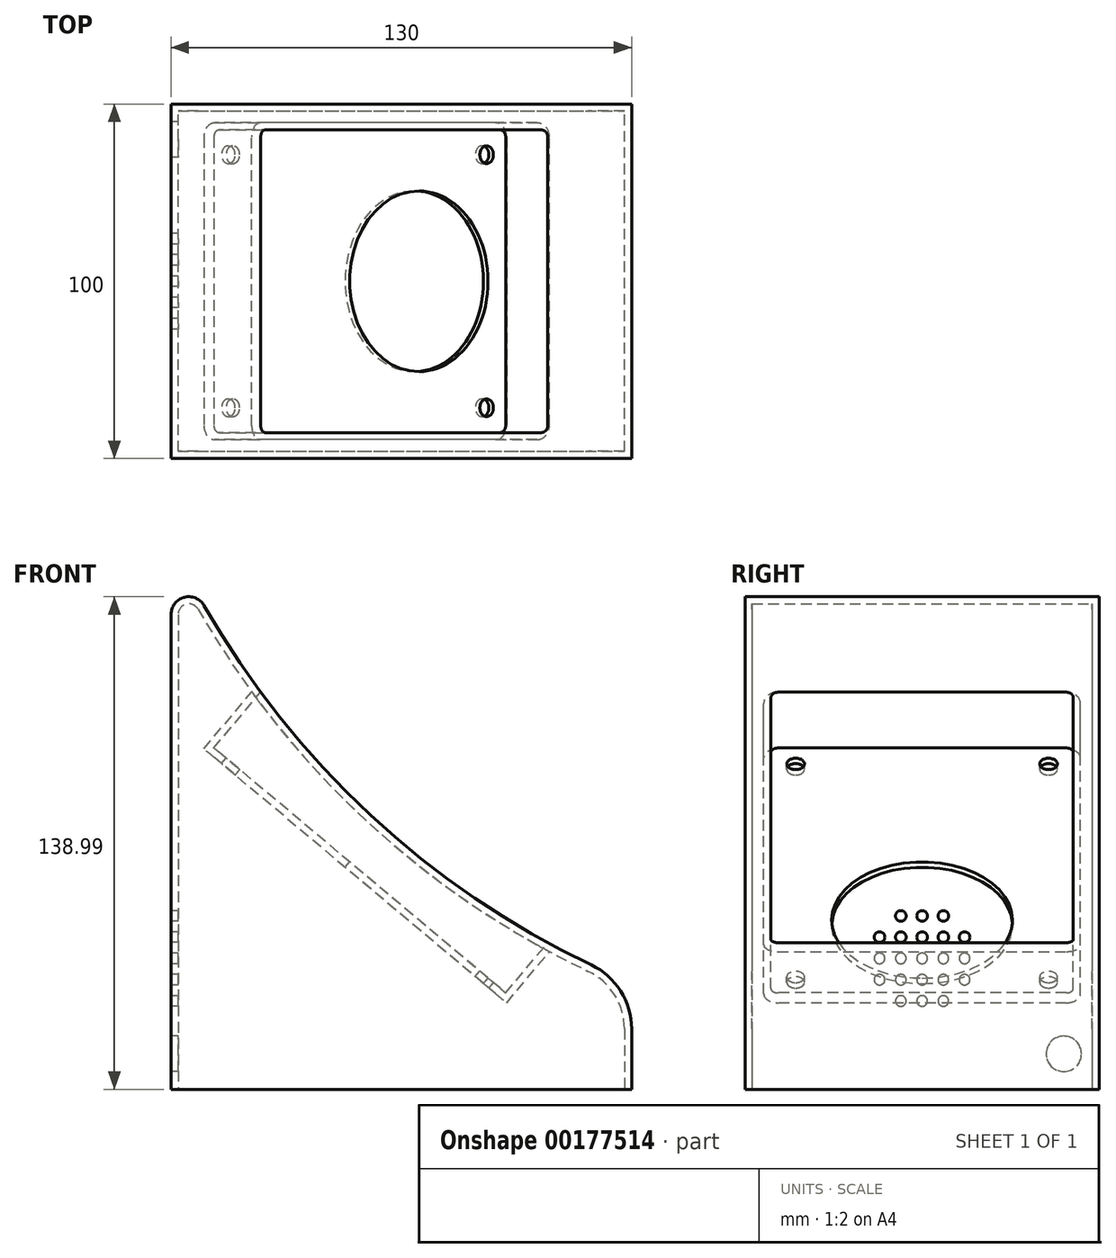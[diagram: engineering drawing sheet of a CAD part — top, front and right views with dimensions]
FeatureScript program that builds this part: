
annotation { "Feature Type Name" : "Feature", "Feature Type Description" : "" }
export const myFeature = defineFeature(function(context is Context, id is Id, definition is map)
    precondition{}
    {
        {
            var Q0;
            Q0=qCreatedBy(makeId("Front.planeOp"),FACE);
            var sketch = newSketch(context, id + "F0", { "sketchPlane" : qUnion([Q0])});
            skLineSegment(sketch, "E0", {"start": v(-84.02, -67.29) * mm, "end": v(45.98, -67.29) * mm});
            skPoint(sketch, "E1.visualSharp", {"position": v(-84.02, 87.14) * mm});
            skPoint(sketch, "E2.visualSharp", {"position": v(45.98, -37.29) * mm});
            skArc(sketch, "E3", {"start": v(-74.68, 69.19) * mm, "mid": v(-23.15, 5.98) * mm, "end": v(45.98, -37.29) * mm});
            skLineSegment(sketch, "E4", {"start": v(-84.02, 66.7) * mm, "end": v(-84.02, -67.29) * mm});
            skLineSegment(sketch, "E5", {"start": v(45.98, -37.29) * mm, "end": v(45.98, -67.29) * mm});
            skArc(sketch, "E6.filletArc", {"start": v(-74.68, 69.19) * mm, "mid": v(-80.3, 71.53) * mm, "end": v(-84.02, 66.7) * mm});
            skSolve(sketch);
        }
        {
            var Q0;
            Q0=makeQuery(id+"F0.imprint","IMPRINT",FACE,{"disambiguationData":[TD([[makeQuery(id+"F0.imprint","IMPRINT",EDGE,{"derivedFrom":sQuery(id+"F0.wireOp",EDGE,"E0")}),1.0]])]});
            extrude(context, id + "F1", {"entities" : qUnion([Q0]), "depth" : 100 * mm, "symmetric" : true});
        }
        {
            var Q0;
            Q0=makeQuery(id+"F1.opExtrude","SWEPT_EDGE",EDGE,{"disambiguationData":[OSD([sQuery(id+"F0.wireOp",EDGE,"E3"),sQuery(id+"F0.wireOp",EDGE,"E5")])]});
            cPlane(context, id + "F2", {"entities" : qUnion([Q0]), "cplaneType" : CPlaneType.LINE_ANGLE, "offset" : 25 * mm, "angle" : 40 * degree, "width" : 150 * mm, "height" : 150 * mm});
        }
        {
            var Q0;
            Q0=qCreatedBy(id+"F2.planeOp",FACE);
            var sketch = newSketch(context, id + "F3", { "sketchPlane" : qUnion([Q0])});
            skLineSegment(sketch, "E7.bottom", {"start": v(31.75, 42.7) * mm, "end": v(-71.75, 42.7) * mm});
            skLineSegment(sketch, "E7.top", {"start": v(31.75, -42.7) * mm, "end": v(-71.75, -42.7) * mm});
            skLineSegment(sketch, "E7.left", {"start": v(33.75, 40.7) * mm, "end": v(33.75, -40.7) * mm});
            skLineSegment(sketch, "E7.right", {"start": v(-73.75, 40.7) * mm, "end": v(-73.75, -40.7) * mm});
            skPoint(sketch, "E7.middle", {"position": v(-20, 0) * mm});
            skPoint(sketch, "E8.visualSharp", {"position": v(-73.75, -42.7) * mm});
            skArc(sketch, "E8.filletArc", {"start": v(-73.75, -40.7) * mm, "mid": v(-73.16, -42.11) * mm, "end": v(-71.75, -42.7) * mm});
            skPoint(sketch, "E9.visualSharp", {"position": v(-73.75, 42.7) * mm});
            skArc(sketch, "E9.filletArc", {"start": v(-71.75, 42.7) * mm, "mid": v(-73.16, 42.11) * mm, "end": v(-73.75, 40.7) * mm});
            skPoint(sketch, "E10.visualSharp", {"position": v(33.75, 42.7) * mm});
            skArc(sketch, "E10.filletArc", {"start": v(33.75, 40.7) * mm, "mid": v(33.16, 42.11) * mm, "end": v(31.75, 42.7) * mm});
            skPoint(sketch, "E11.visualSharp", {"position": v(33.75, -42.7) * mm});
            skArc(sketch, "E11.filletArc", {"start": v(31.75, -42.7) * mm, "mid": v(33.16, -42.11) * mm, "end": v(33.75, -40.7) * mm});
            skCircle(sketch, "E12", {"center": v(1.75, 0) * mm, "radius": 25.5 * mm});
            skCircle(sketch, "E13", {"center": v(-66.75, -35.7) * mm, "radius": 2.5 * mm});
            skCircle(sketch, "E14", {"center": v(-66.75, 35.7) * mm, "radius": 2.5 * mm});
            skCircle(sketch, "E15", {"center": v(26.75, 35.7) * mm, "radius": 2.5 * mm});
            skCircle(sketch, "E16", {"center": v(26.75, -35.7) * mm, "radius": 2.5 * mm});
            skSolve(sketch);
        }
        {
            var Q0;
            Q0=makeQuery(id+"F3.imprint","IMPRINT",FACE,{"disambiguationData":[TD([[makeQuery(id+"F3.imprint","IMPRINT",EDGE,{"derivedFrom":sQuery(id+"F3.wireOp",EDGE,"E7.bottom")}),1.0]])]});
            var Q1;
            Q1=makeQuery(id+"F3.imprint","IMPRINT",FACE,{"disambiguationData":[TD([[makeQuery(id+"F3.imprint","IMPRINT",EDGE,{"derivedFrom":sQuery(id+"F3.wireOp",EDGE,"E12")}),1.0]])]});
            var Q2;
            Q2=makeQuery(id+"F3.imprint","IMPRINT",FACE,{"disambiguationData":[TD([[makeQuery(id+"F3.imprint","IMPRINT",EDGE,{"derivedFrom":sQuery(id+"F3.wireOp",EDGE,"E14")}),1.0]])]});
            var Q3;
            Q3=makeQuery(id+"F3.imprint","IMPRINT",FACE,{"disambiguationData":[TD([[makeQuery(id+"F3.imprint","IMPRINT",EDGE,{"derivedFrom":sQuery(id+"F3.wireOp",EDGE,"E15")}),1.0]])]});
            var Q4;
            Q4=makeQuery(id+"F3.imprint","IMPRINT",FACE,{"disambiguationData":[TD([[makeQuery(id+"F3.imprint","IMPRINT",EDGE,{"derivedFrom":sQuery(id+"F3.wireOp",EDGE,"E16")}),1.0]])]});
            var Q5;
            Q5=makeQuery(id+"F3.imprint","IMPRINT",FACE,{"disambiguationData":[TD([[makeQuery(id+"F3.imprint","IMPRINT",EDGE,{"derivedFrom":sQuery(id+"F3.wireOp",EDGE,"E13")}),1.0]])]});
            extrude(context, id + "F4", {"entities" : qUnion([Q0, Q1, Q2, Q3, Q4, Q5]), "operationType" : NewBodyOperationType.REMOVE, "oppositeDirection" : true, "depth" : 25 * mm});
        }
        {
            var Q0;
            Q0=makeQuery(id+"F1.opExtrude","SWEPT_EDGE",EDGE,{"disambiguationData":[OSD([sQuery(id+"F0.wireOp",EDGE,"E3"),sQuery(id+"F0.wireOp",EDGE,"E5")])]});
            fillet(context, id + "F5", {"entities" : qUnion([Q0]), "radius" : 20 * mm, "tangentPropagation" : true, "allowEdgeOverflow" : false});
        }
        {
            var Q0;
            Q0=makeQuery(id+"F1.opExtrude","SWEPT_FACE",FACE,{"disambiguationData":[OSD([sQuery(id+"F0.wireOp",EDGE,"E0")])]});
            shell(context, id + "F6", {"entities" : qUnion([Q0]), "thickness" : 2 * mm});
        }
        {
            var Q0;
            Q0=makeQuery(id+"F3.imprint","IMPRINT",FACE,{"disambiguationData":[TD([[makeQuery(id+"F3.imprint","IMPRINT",EDGE,{"derivedFrom":sQuery(id+"F3.wireOp",EDGE,"E12")}),1.0]])]});
            var Q1;
            Q1=makeQuery(id+"F3.imprint","IMPRINT",FACE,{"disambiguationData":[TD([[makeQuery(id+"F3.imprint","IMPRINT",EDGE,{"derivedFrom":sQuery(id+"F3.wireOp",EDGE,"E14")}),1.0]])]});
            var Q2;
            Q2=makeQuery(id+"F3.imprint","IMPRINT",FACE,{"disambiguationData":[TD([[makeQuery(id+"F3.imprint","IMPRINT",EDGE,{"derivedFrom":sQuery(id+"F3.wireOp",EDGE,"E13")}),1.0]])]});
            var Q3;
            Q3=makeQuery(id+"F3.imprint","IMPRINT",FACE,{"disambiguationData":[TD([[makeQuery(id+"F3.imprint","IMPRINT",EDGE,{"derivedFrom":sQuery(id+"F3.wireOp",EDGE,"E15")}),1.0]])]});
            var Q4;
            Q4=makeQuery(id+"F3.imprint","IMPRINT",FACE,{"disambiguationData":[TD([[makeQuery(id+"F3.imprint","IMPRINT",EDGE,{"derivedFrom":sQuery(id+"F3.wireOp",EDGE,"E16")}),1.0]])]});
            extrude(context, id + "F7", {"entities" : qUnion([Q0, Q1, Q2, Q3, Q4]), "operationType" : NewBodyOperationType.REMOVE, "oppositeDirection" : true, "depth" : 40 * mm});
        }
        {
            var Q0;
            Q0=makeQuery(id+"F1.opExtrude","SWEPT_FACE",FACE,{"disambiguationData":[OSD([sQuery(id+"F0.wireOp",EDGE,"E4")])]});
            var sketch = newSketch(context, id + "F8", { "sketchPlane" : qUnion([Q0])});
            skCircle(sketch, "E17", {"center": v(0, -30.36) * mm, "radius": 25 * mm, "construction": true});
            skLineSegment(sketch, "E18", {"start": v(0, 0) * mm, "end": v(0, -62.03) * mm, "construction": true});
            skLineSegment(sketch, "E19", {"start": v(-40.29, -30.36) * mm, "end": v(40.58, -30.36) * mm, "construction": true});
            skLineSegment(sketch, "E20", {"start": v(-40.29, -24.36) * mm, "end": v(40.58, -24.36) * mm, "construction": true});
            skLineSegment(sketch, "E21", {"start": v(-40.29, -36.36) * mm, "end": v(40.58, -36.36) * mm, "construction": true});
            skLineSegment(sketch, "E22", {"start": v(-40.29, -42.36) * mm, "end": v(40.58, -42.36) * mm, "construction": true});
            skLineSegment(sketch, "E23", {"start": v(-40.29, -18.36) * mm, "end": v(40.58, -18.36) * mm, "construction": true});
            skLineSegment(sketch, "E24", {"start": v(-6, 0) * mm, "end": v(-6, -62.03) * mm, "construction": true});
            skLineSegment(sketch, "E25", {"start": v(6, 0) * mm, "end": v(6, -62.03) * mm, "construction": true});
            skLineSegment(sketch, "E26", {"start": v(12, 0) * mm, "end": v(12, -62.03) * mm, "construction": true});
            skLineSegment(sketch, "E27", {"start": v(-12, 0) * mm, "end": v(-12, -62.03) * mm, "construction": true});
            skCircle(sketch, "E28", {"center": v(0, -30.36) * mm, "radius": 1.5 * mm});
            skCircle(sketch, "E29", {"center": v(6, -30.36) * mm, "radius": 1.5 * mm});
            skCircle(sketch, "E30", {"center": v(12, -30.36) * mm, "radius": 1.5 * mm});
            skCircle(sketch, "E31", {"center": v(-6, -30.36) * mm, "radius": 1.5 * mm});
            skCircle(sketch, "E32", {"center": v(-12, -30.36) * mm, "radius": 1.5 * mm});
            skCircle(sketch, "E33", {"center": v(0, -24.36) * mm, "radius": 1.5 * mm});
            skCircle(sketch, "E34", {"center": v(6, -24.36) * mm, "radius": 1.5 * mm});
            skCircle(sketch, "E35", {"center": v(-6, -24.36) * mm, "radius": 1.5 * mm});
            skCircle(sketch, "E36", {"center": v(-6, -18.36) * mm, "radius": 1.5 * mm});
            skCircle(sketch, "E37", {"center": v(0, -18.36) * mm, "radius": 1.5 * mm});
            skCircle(sketch, "E38", {"center": v(6, -18.36) * mm, "radius": 1.5 * mm});
            skCircle(sketch, "E39", {"center": v(12, -24.36) * mm, "radius": 1.5 * mm});
            skCircle(sketch, "E40", {"center": v(12, -36.36) * mm, "radius": 1.5 * mm});
            skCircle(sketch, "E41", {"center": v(6, -36.36) * mm, "radius": 1.5 * mm});
            skCircle(sketch, "E42", {"center": v(0, -36.36) * mm, "radius": 1.5 * mm});
            skCircle(sketch, "E43", {"center": v(-6, -36.36) * mm, "radius": 1.5 * mm});
            skCircle(sketch, "E44", {"center": v(-12, -36.36) * mm, "radius": 1.5 * mm});
            skCircle(sketch, "E45", {"center": v(-6, -42.36) * mm, "radius": 1.5 * mm});
            skCircle(sketch, "E46", {"center": v(0, -42.36) * mm, "radius": 1.5 * mm});
            skCircle(sketch, "E47", {"center": v(6, -42.36) * mm, "radius": 1.5 * mm});
            skCircle(sketch, "E48", {"center": v(-12, -24.36) * mm, "radius": 1.5 * mm});
            skCircle(sketch, "E49", {"center": v(-40, -57.29) * mm, "radius": 5 * mm});
            skSolve(sketch);
        }
        {
            var Q0;
            Q0=makeQuery(id+"F8.imprint","IMPRINT",FACE,{"disambiguationData":[TD([[makeQuery(id+"F8.imprint","IMPRINT",EDGE,{"derivedFrom":sQuery(id+"F8.wireOp",EDGE,"E36")}),1.0]])]});
            var Q1;
            Q1=makeQuery(id+"F8.imprint","IMPRINT",FACE,{"disambiguationData":[TD([[makeQuery(id+"F8.imprint","IMPRINT",EDGE,{"derivedFrom":sQuery(id+"F8.wireOp",EDGE,"E37")}),1.0]])]});
            var Q2;
            Q2=makeQuery(id+"F8.imprint","IMPRINT",FACE,{"disambiguationData":[TD([[makeQuery(id+"F8.imprint","IMPRINT",EDGE,{"derivedFrom":sQuery(id+"F8.wireOp",EDGE,"E38")}),1.0]])]});
            var Q3;
            Q3=makeQuery(id+"F8.imprint","IMPRINT",FACE,{"disambiguationData":[TD([[makeQuery(id+"F8.imprint","IMPRINT",EDGE,{"derivedFrom":sQuery(id+"F8.wireOp",EDGE,"E39")}),1.0]])]});
            var Q4;
            Q4=makeQuery(id+"F8.imprint","IMPRINT",FACE,{"disambiguationData":[TD([[makeQuery(id+"F8.imprint","IMPRINT",EDGE,{"derivedFrom":sQuery(id+"F8.wireOp",EDGE,"E34")}),1.0]])]});
            var Q5;
            Q5=makeQuery(id+"F8.imprint","IMPRINT",FACE,{"disambiguationData":[TD([[makeQuery(id+"F8.imprint","IMPRINT",EDGE,{"derivedFrom":sQuery(id+"F8.wireOp",EDGE,"E33")}),1.0]])]});
            var Q6;
            Q6=makeQuery(id+"F8.imprint","IMPRINT",FACE,{"disambiguationData":[TD([[makeQuery(id+"F8.imprint","IMPRINT",EDGE,{"derivedFrom":sQuery(id+"F8.wireOp",EDGE,"E35")}),1.0]])]});
            var Q7;
            Q7=makeQuery(id+"F8.imprint","IMPRINT",FACE,{"disambiguationData":[TD([[makeQuery(id+"F8.imprint","IMPRINT",EDGE,{"derivedFrom":sQuery(id+"F8.wireOp",EDGE,"E48")}),1.0]])]});
            var Q8;
            Q8=makeQuery(id+"F8.imprint","IMPRINT",FACE,{"disambiguationData":[TD([[makeQuery(id+"F8.imprint","IMPRINT",EDGE,{"derivedFrom":sQuery(id+"F8.wireOp",EDGE,"E32")}),1.0]])]});
            var Q9;
            Q9=makeQuery(id+"F8.imprint","IMPRINT",FACE,{"disambiguationData":[TD([[makeQuery(id+"F8.imprint","IMPRINT",EDGE,{"derivedFrom":sQuery(id+"F8.wireOp",EDGE,"E31")}),1.0]])]});
            var Q10;
            Q10=makeQuery(id+"F8.imprint","IMPRINT",FACE,{"disambiguationData":[TD([[makeQuery(id+"F8.imprint","IMPRINT",EDGE,{"derivedFrom":sQuery(id+"F8.wireOp",EDGE,"E28")}),1.0]])]});
            var Q11;
            Q11=makeQuery(id+"F8.imprint","IMPRINT",FACE,{"disambiguationData":[TD([[makeQuery(id+"F8.imprint","IMPRINT",EDGE,{"derivedFrom":sQuery(id+"F8.wireOp",EDGE,"E29")}),1.0]])]});
            var Q12;
            Q12=makeQuery(id+"F8.imprint","IMPRINT",FACE,{"disambiguationData":[TD([[makeQuery(id+"F8.imprint","IMPRINT",EDGE,{"derivedFrom":sQuery(id+"F8.wireOp",EDGE,"E30")}),1.0]])]});
            var Q13;
            Q13=makeQuery(id+"F8.imprint","IMPRINT",FACE,{"disambiguationData":[TD([[makeQuery(id+"F8.imprint","IMPRINT",EDGE,{"derivedFrom":sQuery(id+"F8.wireOp",EDGE,"E41")}),1.0]])]});
            var Q14;
            Q14=makeQuery(id+"F8.imprint","IMPRINT",FACE,{"disambiguationData":[TD([[makeQuery(id+"F8.imprint","IMPRINT",EDGE,{"derivedFrom":sQuery(id+"F8.wireOp",EDGE,"E42")}),1.0]])]});
            var Q15;
            Q15=makeQuery(id+"F8.imprint","IMPRINT",FACE,{"disambiguationData":[TD([[makeQuery(id+"F8.imprint","IMPRINT",EDGE,{"derivedFrom":sQuery(id+"F8.wireOp",EDGE,"E43")}),1.0]])]});
            var Q16;
            Q16=makeQuery(id+"F8.imprint","IMPRINT",FACE,{"disambiguationData":[TD([[makeQuery(id+"F8.imprint","IMPRINT",EDGE,{"derivedFrom":sQuery(id+"F8.wireOp",EDGE,"E44")}),1.0]])]});
            var Q17;
            Q17=makeQuery(id+"F8.imprint","IMPRINT",FACE,{"disambiguationData":[TD([[makeQuery(id+"F8.imprint","IMPRINT",EDGE,{"derivedFrom":sQuery(id+"F8.wireOp",EDGE,"E45")}),1.0]])]});
            var Q18;
            Q18=makeQuery(id+"F8.imprint","IMPRINT",FACE,{"disambiguationData":[TD([[makeQuery(id+"F8.imprint","IMPRINT",EDGE,{"derivedFrom":sQuery(id+"F8.wireOp",EDGE,"E46")}),1.0]])]});
            var Q19;
            Q19=makeQuery(id+"F8.imprint","IMPRINT",FACE,{"disambiguationData":[TD([[makeQuery(id+"F8.imprint","IMPRINT",EDGE,{"derivedFrom":sQuery(id+"F8.wireOp",EDGE,"E47")}),1.0]])]});
            var Q20;
            Q20=makeQuery(id+"F8.imprint","IMPRINT",FACE,{"disambiguationData":[TD([[makeQuery(id+"F8.imprint","IMPRINT",EDGE,{"derivedFrom":sQuery(id+"F8.wireOp",EDGE,"E40")}),1.0]])]});
            var Q21;
            Q21=makeQuery(id+"F8.imprint","IMPRINT",FACE,{"disambiguationData":[TD([[makeQuery(id+"F8.imprint","IMPRINT",EDGE,{"derivedFrom":sQuery(id+"F8.wireOp",EDGE,"E49")}),1.0]])]});
            var Q22;
            Q22=sQuery(id+"F8.wireOp",EDGE,"E48");
            var Q23;
            Q23=sQuery(id+"F8.wireOp",EDGE,"E35");
            var Q24;
            Q24=sQuery(id+"F8.wireOp",EDGE,"E36");
            var Q25;
            Q25=sQuery(id+"F8.wireOp",EDGE,"E37");
            var Q26;
            Q26=sQuery(id+"F8.wireOp",EDGE,"E38");
            var Q27;
            Q27=sQuery(id+"F8.wireOp",EDGE,"E34");
            var Q28;
            Q28=sQuery(id+"F8.wireOp",EDGE,"E33");
            var Q29;
            Q29=sQuery(id+"F8.wireOp",EDGE,"E39");
            var Q30;
            Q30=sQuery(id+"F8.wireOp",EDGE,"E30");
            var Q31;
            Q31=sQuery(id+"F8.wireOp",EDGE,"E29");
            var Q32;
            Q32=sQuery(id+"F8.wireOp",EDGE,"E28");
            var Q33;
            Q33=sQuery(id+"F8.wireOp",EDGE,"E31");
            var Q34;
            Q34=sQuery(id+"F8.wireOp",EDGE,"E32");
            var Q35;
            Q35=sQuery(id+"F8.wireOp",EDGE,"E44");
            var Q36;
            Q36=sQuery(id+"F8.wireOp",EDGE,"E43");
            var Q37;
            Q37=sQuery(id+"F8.wireOp",EDGE,"E42");
            var Q38;
            Q38=sQuery(id+"F8.wireOp",EDGE,"E41");
            var Q39;
            Q39=sQuery(id+"F8.wireOp",EDGE,"E40");
            var Q40;
            Q40=sQuery(id+"F8.wireOp",EDGE,"E47");
            var Q41;
            Q41=sQuery(id+"F8.wireOp",EDGE,"E46");
            var Q42;
            Q42=sQuery(id+"F8.wireOp",EDGE,"E45");
            extrude(context, id + "F9", {"entities" : qUnion([Q0, Q1, Q2, Q3, Q4, Q5, Q6, Q7, Q8, Q9, Q10, Q11, Q12, Q13, Q14, Q15, Q16, Q17, Q18, Q19, Q20, Q21]), "operationType" : NewBodyOperationType.REMOVE, "surfaceEntities" : qUnion([Q22, Q23, Q24, Q25, Q26, Q27, Q28, Q29, Q30, Q31, Q32, Q33, Q34, Q35, Q36, Q37, Q38, Q39, Q40, Q41, Q42]), "oppositeDirection" : true, "depth" : 25 * mm});
        }
    });
